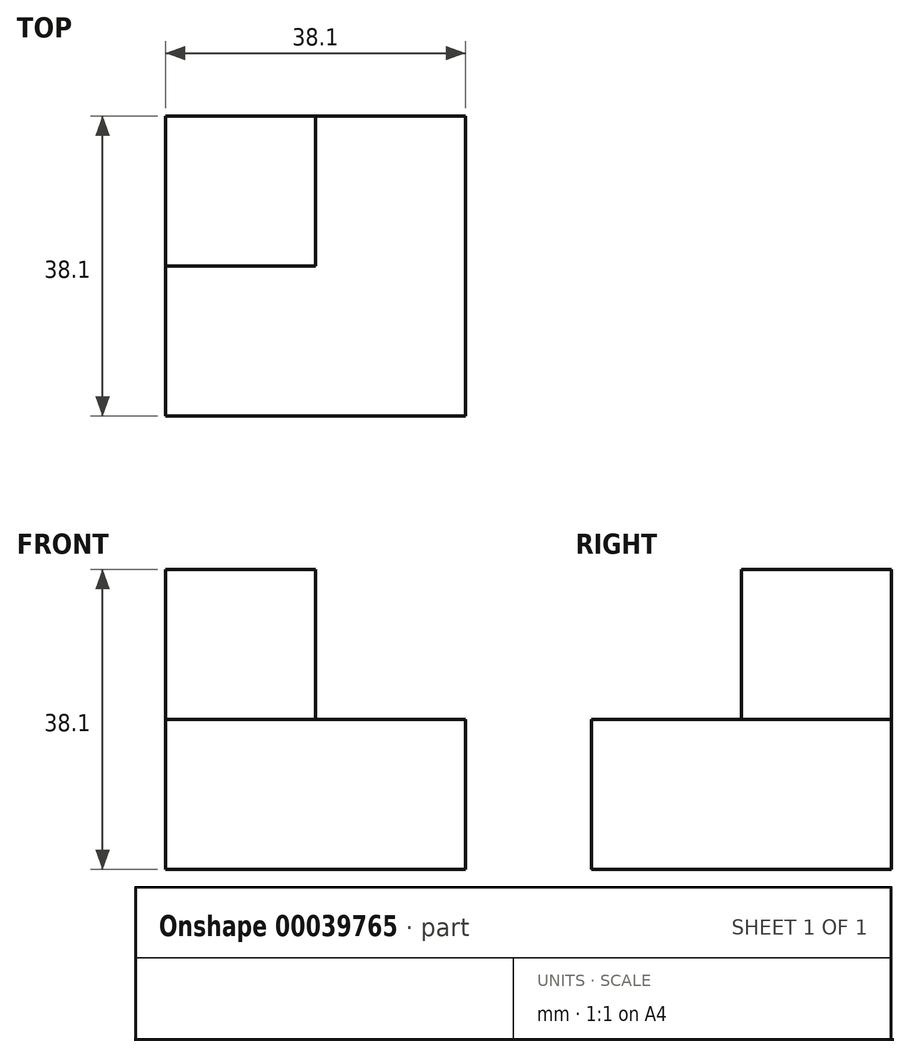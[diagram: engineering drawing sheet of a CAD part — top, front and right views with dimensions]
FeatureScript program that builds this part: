
annotation { "Feature Type Name" : "Feature", "Feature Type Description" : "" }
export const myFeature = defineFeature(function(context is Context, id is Id, definition is map)
    precondition{}
    {
        {
            var Q0;
            Q0=qCreatedBy(makeId("Top.planeOp"),FACE);
            var sketch = newSketch(context, id + "F0", { "sketchPlane" : qUnion([Q0])});
            skLineSegment(sketch, "E0.bottom", {"start": v(0, 0) * mm, "end": v(19.05, 0) * mm});
            skLineSegment(sketch, "E0.top", {"start": v(0, -19.05) * mm, "end": v(19.05, -19.05) * mm});
            skLineSegment(sketch, "E0.left", {"start": v(0, 0) * mm, "end": v(0, -19.05) * mm});
            skLineSegment(sketch, "E0.right", {"start": v(19.05, 0) * mm, "end": v(19.05, -19.05) * mm});
            skSolve(sketch);
        }
        {
            var Q0;
            Q0=makeQuery(id+"F0.imprint","IMPRINT",FACE,{"disambiguationData":[TD([[makeQuery(id+"F0.imprint","IMPRINT",EDGE,{"derivedFrom":sQuery(id+"F0.wireOp",EDGE,"E0.bottom")}),-1.0]])]});
            extrude(context, id + "F1", {"entities" : qUnion([Q0]), "depth" : 19.05 * mm});
        }
        {
            var Q0;
            Q0=makeQuery(id+"F1.opExtrude","CAP_FACE",FACE,{"disambiguationData":[OSD([sQuery(id+"F0.wireOp",EDGE,"E0.bottom"),sQuery(id+"F0.wireOp",EDGE,"E0.top"),sQuery(id+"F0.wireOp",EDGE,"E0.left"),sQuery(id+"F0.wireOp",EDGE,"E0.right")])],"isStart":false});
            extrude(context, id + "F2", {"entities" : qUnion([Q0]), "operationType" : NewBodyOperationType.ADD, "depth" : 19.05 * mm});
        }
        {
            var Q0;
            {var subQ0=sQuery(id+"F0.wireOp",EDGE,"E0.top");Q0=makeQuery(id+"F2.boolean.opBoolean","MERGE",FACE,{"derivedFrom":[makeQuery(id+"F1.opExtrude","SWEPT_FACE",FACE,{"disambiguationData":[OSD([subQ0])]}),makeQuery(id+"F2.opExtrude","SWEPT_FACE",FACE,{"disambiguationData":[OSD([subQ0])]})]});}
            var sketch = newSketch(context, id + "F3", { "sketchPlane" : qUnion([Q0])});
            skLineSegment(sketch, "E1.bottom", {"start": v(0, 19.05) * mm, "end": v(19.05, 19.05) * mm});
            skLineSegment(sketch, "E1.top", {"start": v(0, 0) * mm, "end": v(19.05, 0) * mm});
            skLineSegment(sketch, "E1.left", {"start": v(0, 19.05) * mm, "end": v(0, 0) * mm});
            skLineSegment(sketch, "E1.right", {"start": v(19.05, 19.05) * mm, "end": v(19.05, 0) * mm});
            skSolve(sketch);
        }
        {
            var Q0;
            Q0=makeQuery(id+"F3.imprint","IMPRINT",FACE,{"disambiguationData":[TD([[makeQuery(id+"F3.imprint","IMPRINT",EDGE,{"derivedFrom":sQuery(id+"F3.wireOp",EDGE,"E1.bottom")}),-1.0]])]});
            extrude(context, id + "F4", {"entities" : qUnion([Q0]), "operationType" : NewBodyOperationType.ADD, "depth" : 19.05 * mm});
        }
        {
            var Q0;
            {var subQ0=sQuery(id+"F0.wireOp",EDGE,"E0.right");Q0=makeQuery(id+"F4.boolean.opBoolean","MERGE",FACE,{"derivedFrom":[makeQuery(id+"F2.boolean.opBoolean","MERGE",FACE,{"derivedFrom":[makeQuery(id+"F1.opExtrude","SWEPT_FACE",FACE,{"disambiguationData":[OSD([subQ0])]}),makeQuery(id+"F2.opExtrude","SWEPT_FACE",FACE,{"disambiguationData":[OSD([subQ0])]})]}),makeQuery(id+"F4.opExtrude","SWEPT_FACE",FACE,{"disambiguationData":[OSD([sQuery(id+"F3.wireOp",EDGE,"E1.right")])]})]});}
            var sketch = newSketch(context, id + "F5", { "sketchPlane" : qUnion([Q0])});
            skLineSegment(sketch, "E2.bottom", {"start": v(-38.1, 0) * mm, "end": v(-19.05, 0) * mm});
            skLineSegment(sketch, "E2.top", {"start": v(-38.1, 19.05) * mm, "end": v(-19.05, 19.05) * mm});
            skLineSegment(sketch, "E2.left", {"start": v(-38.1, 0) * mm, "end": v(-38.1, 19.05) * mm});
            skLineSegment(sketch, "E2.right", {"start": v(-19.05, 0) * mm, "end": v(-19.05, 19.05) * mm});
            skSolve(sketch);
        }
        {
            var Q0;
            Q0=makeQuery(id+"F5.imprint","IMPRINT",FACE,{"disambiguationData":[TD([[makeQuery(id+"F5.imprint","IMPRINT",EDGE,{"derivedFrom":sQuery(id+"F5.wireOp",EDGE,"E2.bottom")}),-1.0]])]});
            extrude(context, id + "F6", {"entities" : qUnion([Q0]), "operationType" : NewBodyOperationType.ADD, "depth" : 19.05 * mm});
        }
        {
            var Q0;
            Q0=makeQuery(id+"F6.opExtrude","SWEPT_FACE",FACE,{"disambiguationData":[OSD([sQuery(id+"F5.wireOp",EDGE,"E2.right")])]});
            extrude(context, id + "F7", {"entities" : qUnion([Q0]), "operationType" : NewBodyOperationType.ADD, "depth" : 19.05 * mm});
        }
    });
